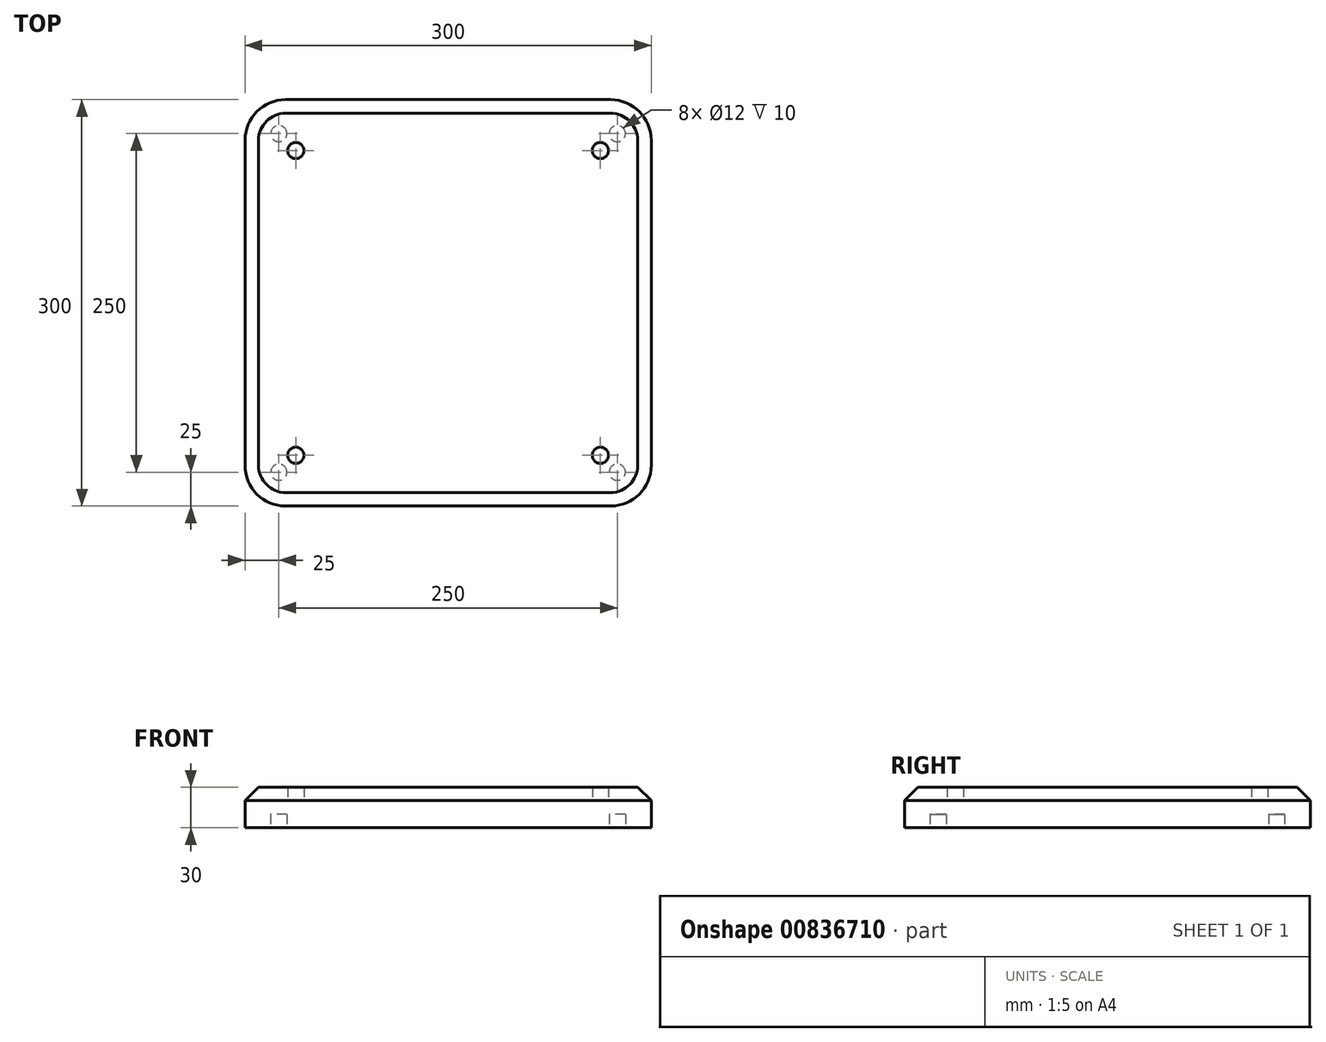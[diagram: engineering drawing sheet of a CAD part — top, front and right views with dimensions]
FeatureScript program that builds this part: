
annotation { "Feature Type Name" : "Feature", "Feature Type Description" : "" }
export const myFeature = defineFeature(function(context is Context, id is Id, definition is map)
    precondition{}
    {
        {
            var Q0;
            Q0=qCreatedBy(makeId("Top.planeOp"),FACE);
            var sketch = newSketch(context, id + "F0", { "sketchPlane" : qUnion([Q0])});
            skLineSegment(sketch, "E0.bottom", {"start": v(-120, 150) * mm, "end": v(120, 150) * mm});
            skLineSegment(sketch, "E0.top", {"start": v(-120, -150) * mm, "end": v(120, -150) * mm});
            skLineSegment(sketch, "E0.left", {"start": v(-150, 120) * mm, "end": v(-150, -120) * mm});
            skLineSegment(sketch, "E0.right", {"start": v(150, 120) * mm, "end": v(150, -120) * mm});
            skCircle(sketch, "E1", {"center": v(-112.5, 112.5) * mm, "radius": 6 * mm});
            skCircle(sketch, "E2", {"center": v(-112.5, -112.5) * mm, "radius": 6 * mm});
            skCircle(sketch, "E3", {"center": v(112.5, -112.5) * mm, "radius": 6 * mm});
            skCircle(sketch, "E4", {"center": v(112.5, 112.5) * mm, "radius": 6 * mm});
            skPoint(sketch, "E5.visualSharp", {"position": v(-150, 150) * mm});
            skArc(sketch, "E5.filletArc", {"start": v(-120, 150) * mm, "mid": v(-141.21, 141.21) * mm, "end": v(-150, 120) * mm});
            skPoint(sketch, "E6.visualSharp", {"position": v(150, 150) * mm});
            skArc(sketch, "E6.filletArc", {"start": v(150, 120) * mm, "mid": v(141.21, 141.21) * mm, "end": v(120, 150) * mm});
            skPoint(sketch, "E7.visualSharp", {"position": v(-150, -150) * mm});
            skArc(sketch, "E7.filletArc", {"start": v(-150, -120) * mm, "mid": v(-141.21, -141.21) * mm, "end": v(-120, -150) * mm});
            skPoint(sketch, "E8.visualSharp", {"position": v(150, -150) * mm});
            skArc(sketch, "E8.filletArc", {"start": v(120, -150) * mm, "mid": v(141.21, -141.21) * mm, "end": v(150, -120) * mm});
            skCircle(sketch, "E9", {"center": v(-125, 125) * mm, "radius": 6 * mm});
            skCircle(sketch, "E10", {"center": v(-125, -125) * mm, "radius": 6 * mm});
            skCircle(sketch, "E11", {"center": v(125, -125) * mm, "radius": 6 * mm});
            skCircle(sketch, "E12", {"center": v(125, 125) * mm, "radius": 6 * mm});
            skSolve(sketch);
        }
        {
            var Q0;
            Q0 = qSketchRegion(id + "F0", true);
            extrude(context, id + "F1", {"entities" : qUnion([Q0]), "depth" : 15 * mm, "offsetDistance" : 25 * mm, "hasSecondDirection" : true, "secondDirectionOppositeDirection" : true, "secondDirectionDepth" : 15 * mm});
        }
        {
            var Q0;
            Q0=makeQuery(id+"F1.opExtrude","CAP_EDGE",EDGE,{"disambiguationData":[OSD([sQuery(id+"F0.wireOp",EDGE,"E0.bottom")])],"isStart":false});
            var Q1;
            Q1=makeQuery(id+"F1.opExtrude","CAP_EDGE",EDGE,{"disambiguationData":[OSD([sQuery(id+"F0.wireOp",EDGE,"E5.filletArc")])],"isStart":false});
            var Q2;
            Q2=makeQuery(id+"F1.opExtrude","CAP_EDGE",EDGE,{"disambiguationData":[OSD([sQuery(id+"F0.wireOp",EDGE,"E0.left")])],"isStart":false});
            var Q3;
            Q3=makeQuery(id+"F1.opExtrude","CAP_EDGE",EDGE,{"disambiguationData":[OSD([sQuery(id+"F0.wireOp",EDGE,"E0.top")])],"isStart":false});
            var Q4;
            Q4=makeQuery(id+"F1.opExtrude","CAP_EDGE",EDGE,{"disambiguationData":[OSD([sQuery(id+"F0.wireOp",EDGE,"E7.filletArc")])],"isStart":false});
            var Q5;
            Q5=makeQuery(id+"F1.opExtrude","CAP_EDGE",EDGE,{"disambiguationData":[OSD([sQuery(id+"F0.wireOp",EDGE,"E8.filletArc")])],"isStart":false});
            var Q6;
            Q6=makeQuery(id+"F1.opExtrude","CAP_EDGE",EDGE,{"disambiguationData":[OSD([sQuery(id+"F0.wireOp",EDGE,"E0.right")])],"isStart":false});
            var Q7;
            Q7=makeQuery(id+"F1.opExtrude","CAP_EDGE",EDGE,{"disambiguationData":[OSD([sQuery(id+"F0.wireOp",EDGE,"E6.filletArc")])],"isStart":false});
            chamfer(context, id + "F2", {"entities" : qUnion([Q0, Q1, Q2, Q3, Q4, Q5, Q6, Q7]), "width" : 10 * mm, "tangentPropagation" : true});
        }
        {
            var Q0;
            Q0=makeQuery(id+"F0.imprint","IMPRINT",FACE,{"disambiguationData":[TD([[makeQuery(id+"F0.imprint","IMPRINT",EDGE,{"derivedFrom":sQuery(id+"F0.wireOp",EDGE,"E1")}),1.0]])]});
            var Q1;
            Q1=makeQuery(id+"F0.imprint","IMPRINT",FACE,{"disambiguationData":[TD([[makeQuery(id+"F0.imprint","IMPRINT",EDGE,{"derivedFrom":sQuery(id+"F0.wireOp",EDGE,"E4")}),1.0]])]});
            var Q2;
            Q2=makeQuery(id+"F0.imprint","IMPRINT",FACE,{"disambiguationData":[TD([[makeQuery(id+"F0.imprint","IMPRINT",EDGE,{"derivedFrom":sQuery(id+"F0.wireOp",EDGE,"E3")}),1.0]])]});
            var Q3;
            Q3=makeQuery(id+"F0.imprint","IMPRINT",FACE,{"disambiguationData":[TD([[makeQuery(id+"F0.imprint","IMPRINT",EDGE,{"derivedFrom":sQuery(id+"F0.wireOp",EDGE,"E2")}),1.0]])]});
            extrude(context, id + "F3", {"entities" : qUnion([Q0, Q1, Q2, Q3]), "operationType" : NewBodyOperationType.ADD, "depth" : 5 * mm, "offsetDistance" : 25 * mm, "hasSecondDirection" : true, "secondDirectionOppositeDirection" : true, "secondDirectionDepth" : 15 * mm});
        }
        {
            var Q0;
            Q0=makeQuery(id+"F0.imprint","IMPRINT",FACE,{"disambiguationData":[TD([[makeQuery(id+"F0.imprint","IMPRINT",EDGE,{"derivedFrom":sQuery(id+"F0.wireOp",EDGE,"E12")}),1.0]])]});
            var Q1;
            Q1=makeQuery(id+"F0.imprint","IMPRINT",FACE,{"disambiguationData":[TD([[makeQuery(id+"F0.imprint","IMPRINT",EDGE,{"derivedFrom":sQuery(id+"F0.wireOp",EDGE,"E9")}),1.0]])]});
            var Q2;
            Q2=makeQuery(id+"F0.imprint","IMPRINT",FACE,{"disambiguationData":[TD([[makeQuery(id+"F0.imprint","IMPRINT",EDGE,{"derivedFrom":sQuery(id+"F0.wireOp",EDGE,"E10")}),1.0]])]});
            var Q3;
            Q3=makeQuery(id+"F0.imprint","IMPRINT",FACE,{"disambiguationData":[TD([[makeQuery(id+"F0.imprint","IMPRINT",EDGE,{"derivedFrom":sQuery(id+"F0.wireOp",EDGE,"E11")}),1.0]])]});
            extrude(context, id + "F4", {"entities" : qUnion([Q0, Q1, Q2, Q3]), "operationType" : NewBodyOperationType.ADD, "depth" : 15 * mm, "offsetDistance" : 25 * mm, "hasSecondDirection" : true, "secondDirectionOppositeDirection" : true, "secondDirectionDepth" : 5 * mm});
        }
    });
